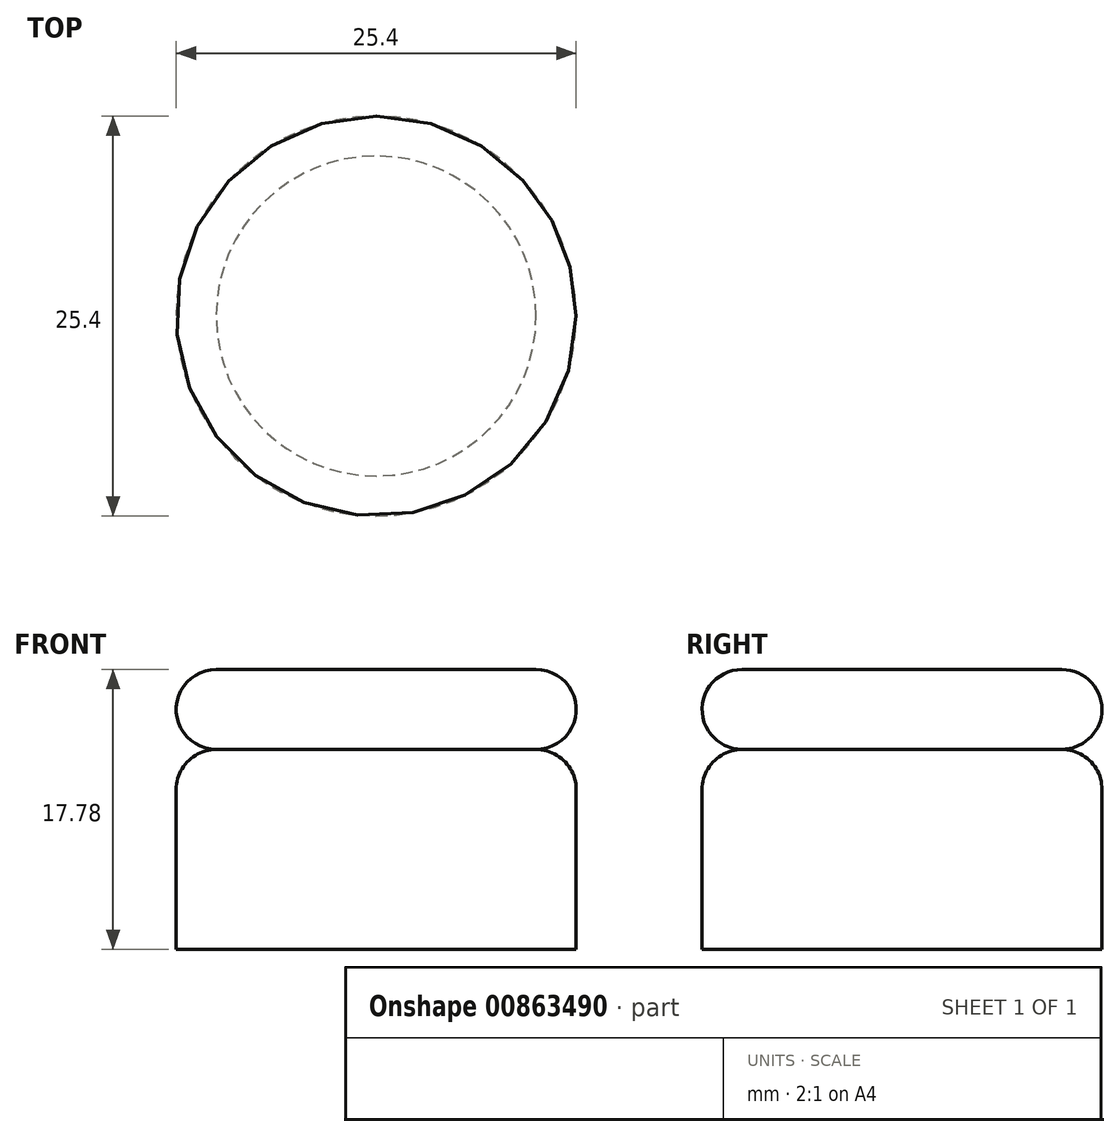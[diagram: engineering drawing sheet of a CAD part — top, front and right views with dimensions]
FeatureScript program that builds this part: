
annotation { "Feature Type Name" : "Feature", "Feature Type Description" : "" }
export const myFeature = defineFeature(function(context is Context, id is Id, definition is map)
    precondition{}
    {
        {
            var Q0;
            Q0=qCreatedBy(makeId("Front.planeOp"),FACE);
            var sketch = newSketch(context, id + "F0", { "sketchPlane" : qUnion([Q0])});
            skLineSegment(sketch, "E0", {"start": v(0, 0) * mm, "end": v(12.7, 0) * mm});
            skLineSegment(sketch, "E1", {"start": v(12.7, 17.78) * mm, "end": v(0, 17.78) * mm});
            skLineSegment(sketch, "E2", {"start": v(0, 17.78) * mm, "end": v(0, 0) * mm});
            skLineSegment(sketch, "E3", {"start": v(12.7, 0) * mm, "end": v(12.7, 10.16) * mm});
            skLineSegment(sketch, "E4", {"start": v(12.7, 17.78) * mm, "end": v(12.7, 15.24) * mm});
            skArc(sketch, "E5", {"start": v(12.7, 10.16) * mm, "mid": v(11.96, 11.96) * mm, "end": v(10.16, 12.7) * mm});
            skArc(sketch, "E6", {"start": v(10.16, 12.7) * mm, "mid": v(11.96, 13.44) * mm, "end": v(12.7, 15.24) * mm});
            skSolve(sketch);
        }
        {
            var Q0;
            Q0=makeQuery(id+"F0.imprint","IMPRINT",FACE,{"disambiguationData":[TD([[makeQuery(id+"F0.imprint","IMPRINT",EDGE,{"derivedFrom":sQuery(id+"F0.wireOp",EDGE,"E0")}),1.0]])]});
            var Q1;
            Q1=sQuery(id+"F0.wireOp",EDGE,"E2");
            revolve(context, id + "F1", {"surfaceOperationType" : NewSurfaceOperationType.NEW, "entities" : qUnion([Q0]), "axis" : qUnion([Q1]), "revolveType" : RevolveType.FULL});
        }
        {
            var Q0;
            Q0=makeQuery(id+"F1.opRevolve","SWEPT_EDGE",EDGE,{"disambiguationData":[OSD([sQuery(id+"F0.wireOp",EDGE,"E1"),sQuery(id+"F0.wireOp",EDGE,"E4")])]});
            fillet(context, id + "F2", {"entities" : qUnion([Q0]), "radius" : 2.54 * mm, "tangentPropagation" : true, "allowEdgeOverflow" : false});
        }
    });
